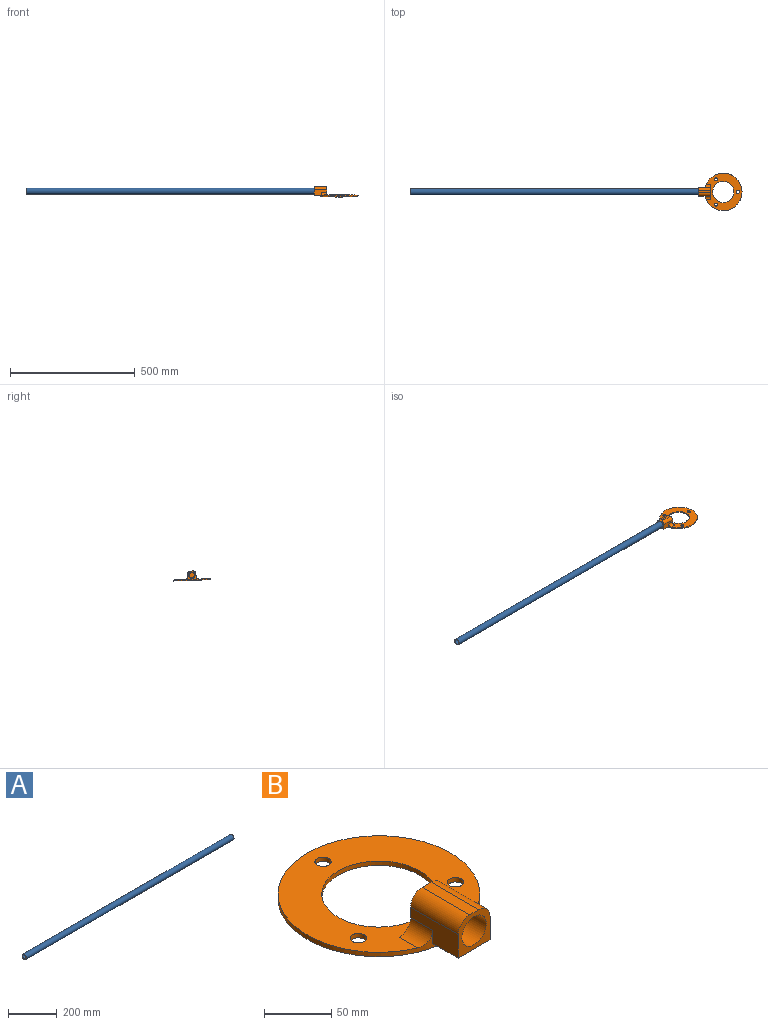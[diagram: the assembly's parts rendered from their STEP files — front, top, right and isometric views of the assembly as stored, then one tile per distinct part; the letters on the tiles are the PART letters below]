
ASSEMBLY  parts=2 mates=1
PART A: 4 faces, bbox 1200x25.4x25.4 mm
  f0: cylinder r=12.7mm len=1200mm, axis (-1,0,0), area 95755.7mm2, adj f1,f2
  f1: plane 25.4x25.4mm, normal (1,0,0), area 179.9mm2, adj f0,f3
  f2: plane 25.4x25.4mm, normal (-1,0,0), area 179.9mm2, adj f0,f3
  f3: cylinder r=10.2mm len=1200mm, axis (-1,0,0), area 76906.2mm2, adj f1,f2
PART B: 19 faces, bbox 150x175x37.4 mm
  f0: plane 150x144.29mm, normal (0,0,1), area 10330.2mm2, adj f1,f2,f3,f4,f5,f11,f17,f18
  f1: cylinder r=42.5mm len=85mm, axis (0,0,-1), area 1068.1mm2, adj f0,f6
  f2: cylinder r=6mm len=12mm, axis (0,0,-1), area 150.8mm2, adj f0,f6
  f3: cylinder r=6mm len=12mm, axis (0,0,-1), area 150.8mm2, adj f0,f6
  f4: cylinder r=6mm len=12mm, axis (0,0,-1), area 150.8mm2, adj f0,f6
  f5: cylinder r=75mm len=150mm, axis (0,0,-1), area 1948.9mm2, adj f0,f6,f7,f8,f10,f17,f18
  f6: plane 150x150mm, normal (0,0,-1), area 11657.7mm2, adj f1,f2,f3,f4,f5
  f7: plane 33.4x26.88mm, normal (0,0,-1), area 855.9mm2, adj f5,f8,f9,f10
  f8: plane 50x21.4mm, normal (-1,0,0), area 792.6mm2, adj f5,f7,f9,f11,f14,f17
  f9: plane 33.4x33.4mm, normal (0,-1,0), area 541mm2, adj f7,f8,f10,f12,f13,f14,f15
  f10: plane 50x21.4mm, normal (1,0,0), area 792.6mm2, adj f5,f7,f9,f11,f13,f18
  f11: plane 57.4x33.4mm, normal (0,1,0), area 1115.6mm2, adj f0,f8,f10,f12,f13,f14,f17,f18
  f12: plane 50x9.4mm, normal (0,0,1), area 470mm2, adj f9,f11,f13,f14
  f13: cylinder r=12mm len=50mm, axis (0,-1,0), area 942.5mm2, adj f9,f10,f11,f12
  f14: cylinder r=12mm len=50mm, axis (0,1,0), area 942.5mm2, adj f8,f9,f11,f12
  f15: cylinder r=12.78mm len=45mm, axis (0,-1,0), area 3612mm2, adj f9,f16
  f16: plane 25.55x25.55mm, normal (0,-1,0), area 512.7mm2, adj f15
  f17: cylinder r=12mm len=23.12mm, axis (0,-1,0), area 412.4mm2, adj f0,f5,f8,f11
  f18: cylinder r=12mm len=23.12mm, axis (0,1,0), area 412.4mm2, adj f0,f5,f10,f11
PLACE A at identity fixed
PLACE B rot(axis=(-0.02,-0.02,-1),90deg) t=(656.11,-0.75,-20.69)mm
MATE cylindrical B.f15 <-> A.f0  axis (-1,0,0) through (556.11,0,0)mm
